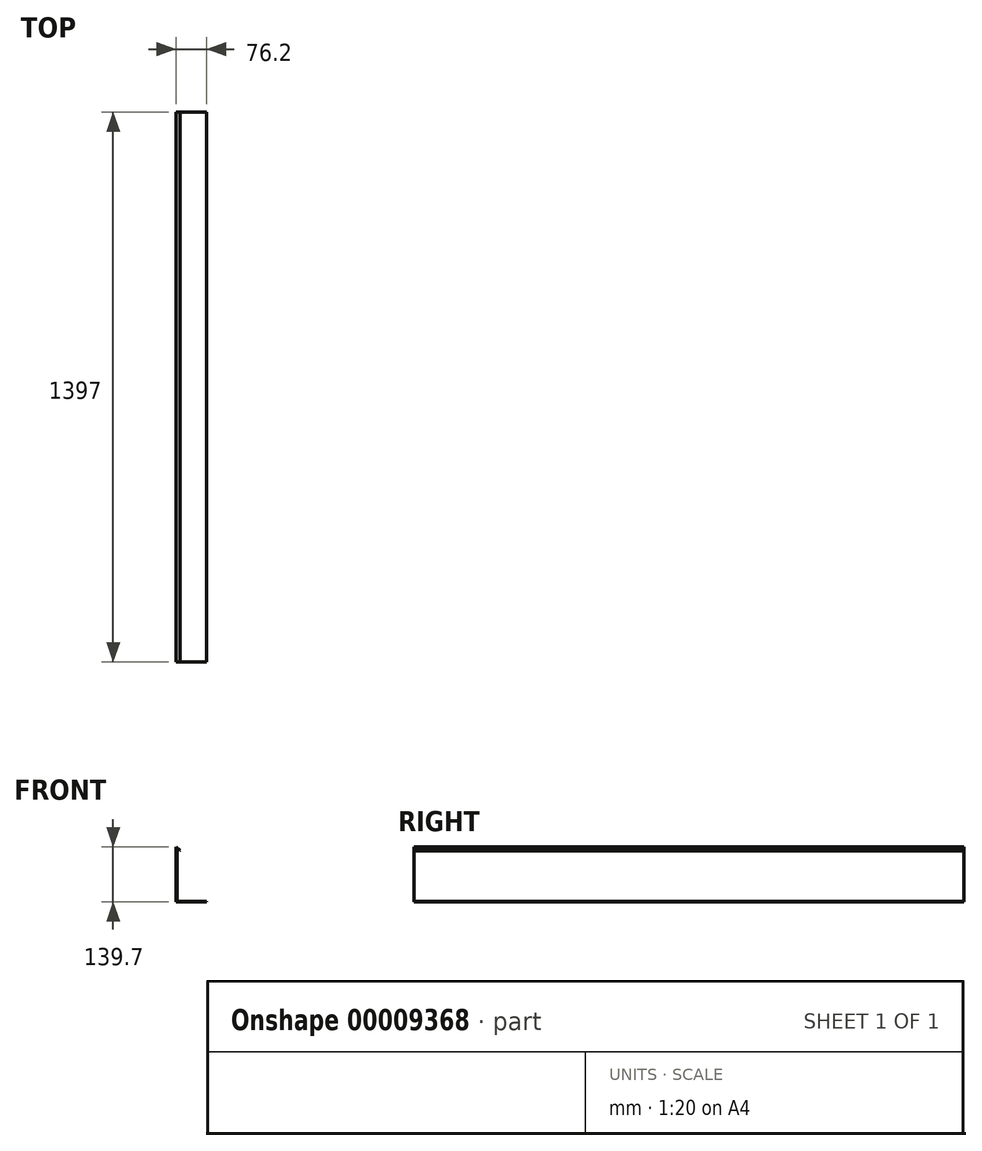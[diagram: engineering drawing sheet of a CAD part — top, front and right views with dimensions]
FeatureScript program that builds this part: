
annotation { "Feature Type Name" : "Feature", "Feature Type Description" : "" }
export const myFeature = defineFeature(function(context is Context, id is Id, definition is map)
    precondition{}
    {
        {
            var Q0;
            Q0=qCreatedBy(makeId("Front.planeOp"),FACE);
            var sketch = newSketch(context, id + "F0", { "sketchPlane" : qUnion([Q0])});
            skLineSegment(sketch, "E0", {"start": v(8.98, 130.72) * mm, "end": v(0, 139.7) * mm});
            skLineSegment(sketch, "E1", {"start": v(0, 139.7) * mm, "end": v(0, 0) * mm});
            skLineSegment(sketch, "E2", {"start": v(0, 0) * mm, "end": v(76.2, 0) * mm});
            skLineSegment(sketch, "E3", {"start": v(76.2, 0) * mm, "end": v(76.2, 1.31) * mm});
            skLineSegment(sketch, "E4", {"start": v(76.2, 1.31) * mm, "end": v(1.31, 1.31) * mm});
            skLineSegment(sketch, "E5", {"start": v(1.31, 1.31) * mm, "end": v(1.31, 136.54) * mm});
            skLineSegment(sketch, "E6", {"start": v(1.31, 136.54) * mm, "end": v(8.05, 129.8) * mm});
            skLineSegment(sketch, "E7", {"start": v(8.05, 129.8) * mm, "end": v(8.98, 130.72) * mm});
            skSolve(sketch);
        }
        {
            var Q0;
            Q0=makeQuery(id+"F0.imprint","IMPRINT",FACE,{"disambiguationData":[TD([[makeQuery(id+"F0.imprint","IMPRINT",EDGE,{"derivedFrom":sQuery(id+"F0.wireOp",EDGE,"E0")}),1.0]])]});
            extrude(context, id + "F1", {"entities" : qUnion([Q0]), "depth" : 1397 * mm});
        }
    });
